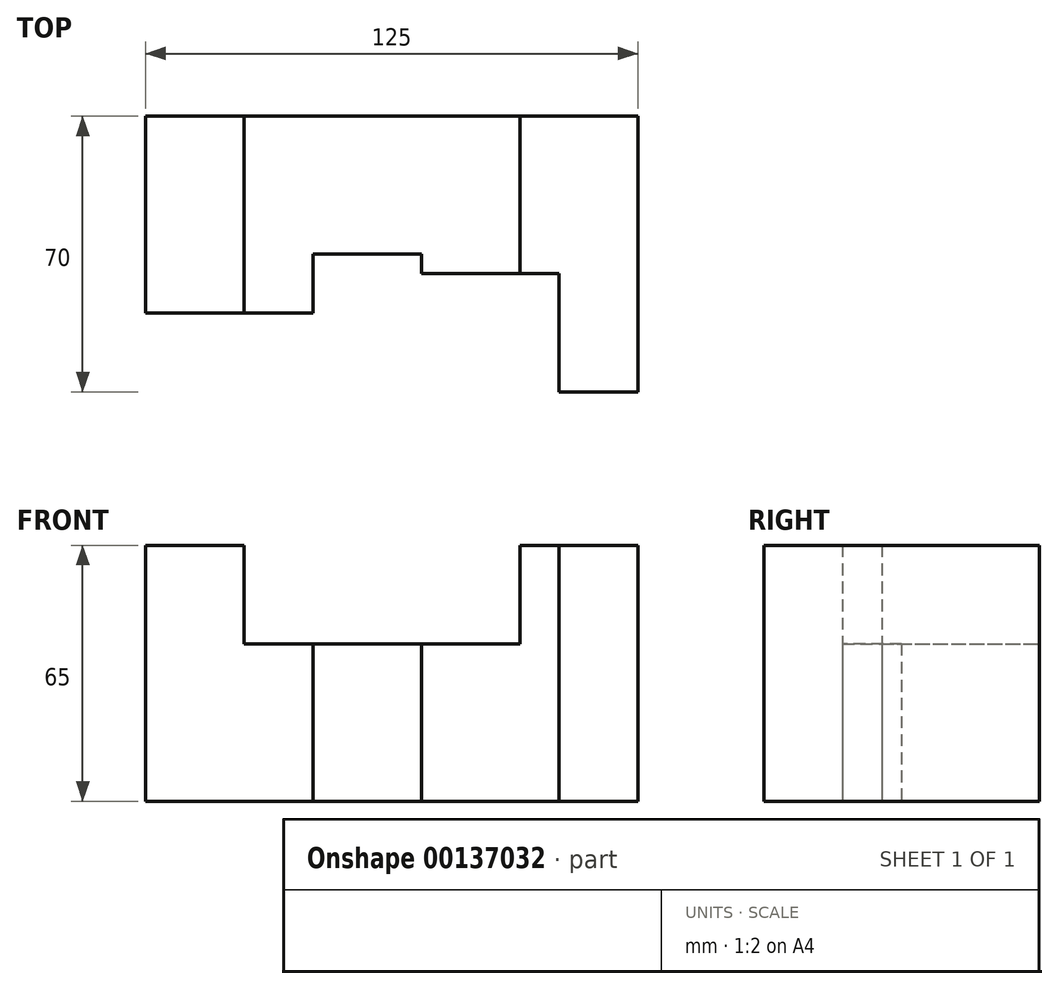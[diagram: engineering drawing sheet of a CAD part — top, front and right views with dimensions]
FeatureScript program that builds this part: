
annotation { "Feature Type Name" : "Feature", "Feature Type Description" : "" }
export const myFeature = defineFeature(function(context is Context, id is Id, definition is map)
    precondition{}
    {
        {
            var Q0;
            Q0=qCreatedBy(makeId("Top.planeOp"),FACE);
            var sketch = newSketch(context, id + "F0", { "sketchPlane" : qUnion([Q0])});
            skLineSegment(sketch, "E0", {"start": v(0, 0) * mm, "end": v(125, 0) * mm});
            skLineSegment(sketch, "E1", {"start": v(125, 0) * mm, "end": v(125, -70) * mm});
            skLineSegment(sketch, "E2", {"start": v(125, -70) * mm, "end": v(105, -70) * mm});
            skLineSegment(sketch, "E3", {"start": v(105, -70) * mm, "end": v(105, -40) * mm});
            skLineSegment(sketch, "E4", {"start": v(105, -40) * mm, "end": v(70, -40) * mm});
            skLineSegment(sketch, "E5", {"start": v(70, -40) * mm, "end": v(70, -35) * mm});
            skLineSegment(sketch, "E6", {"start": v(70, -35) * mm, "end": v(42.5, -35) * mm});
            skLineSegment(sketch, "E7", {"start": v(42.5, -35) * mm, "end": v(42.5, -50) * mm});
            skLineSegment(sketch, "E8", {"start": v(42.5, -50) * mm, "end": v(0, -50) * mm});
            skLineSegment(sketch, "E9", {"start": v(0, -50) * mm, "end": v(0, 0) * mm});
            skLineSegment(sketch, "E10", {"start": v(25, -50) * mm, "end": v(25, 0) * mm});
            skLineSegment(sketch, "E11", {"start": v(95, -40) * mm, "end": v(95, 0) * mm});
            skSolve(sketch);
        }
        {
            var Q0;
            {var subQ0=sQuery(id+"F0.wireOp",EDGE,"E5");Q0=makeQuery(id+"F0.imprint","IMPRINT",FACE,{"disambiguationData":[TD([[makeQuery(id+"F0.imprint","IMPRINT",EDGE,{"derivedFrom":subQ0}),-1.0]])]});}
            extrude(context, id + "F1", {"entities" : qUnion([Q0]), "depth" : 40 * mm});
        }
        {
            var Q0;
            {var subQ0=sQuery(id+"F0.wireOp",EDGE,"E9");Q0=makeQuery(id+"F0.imprint","IMPRINT",FACE,{"disambiguationData":[TD([[makeQuery(id+"F0.imprint","IMPRINT",EDGE,{"derivedFrom":subQ0}),-1.0]])]});}
            var Q1;
            {var subQ1=sQuery(id+"F0.wireOp",EDGE,"E1");Q1=makeQuery(id+"F0.imprint","IMPRINT",FACE,{"disambiguationData":[TD([[makeQuery(id+"F0.imprint","IMPRINT",EDGE,{"derivedFrom":subQ1}),-1.0]])]});}
            extrude(context, id + "F2", {"entities" : qUnion([Q0, Q1]), "operationType" : NewBodyOperationType.ADD, "depth" : 65 * mm});
        }
    });
